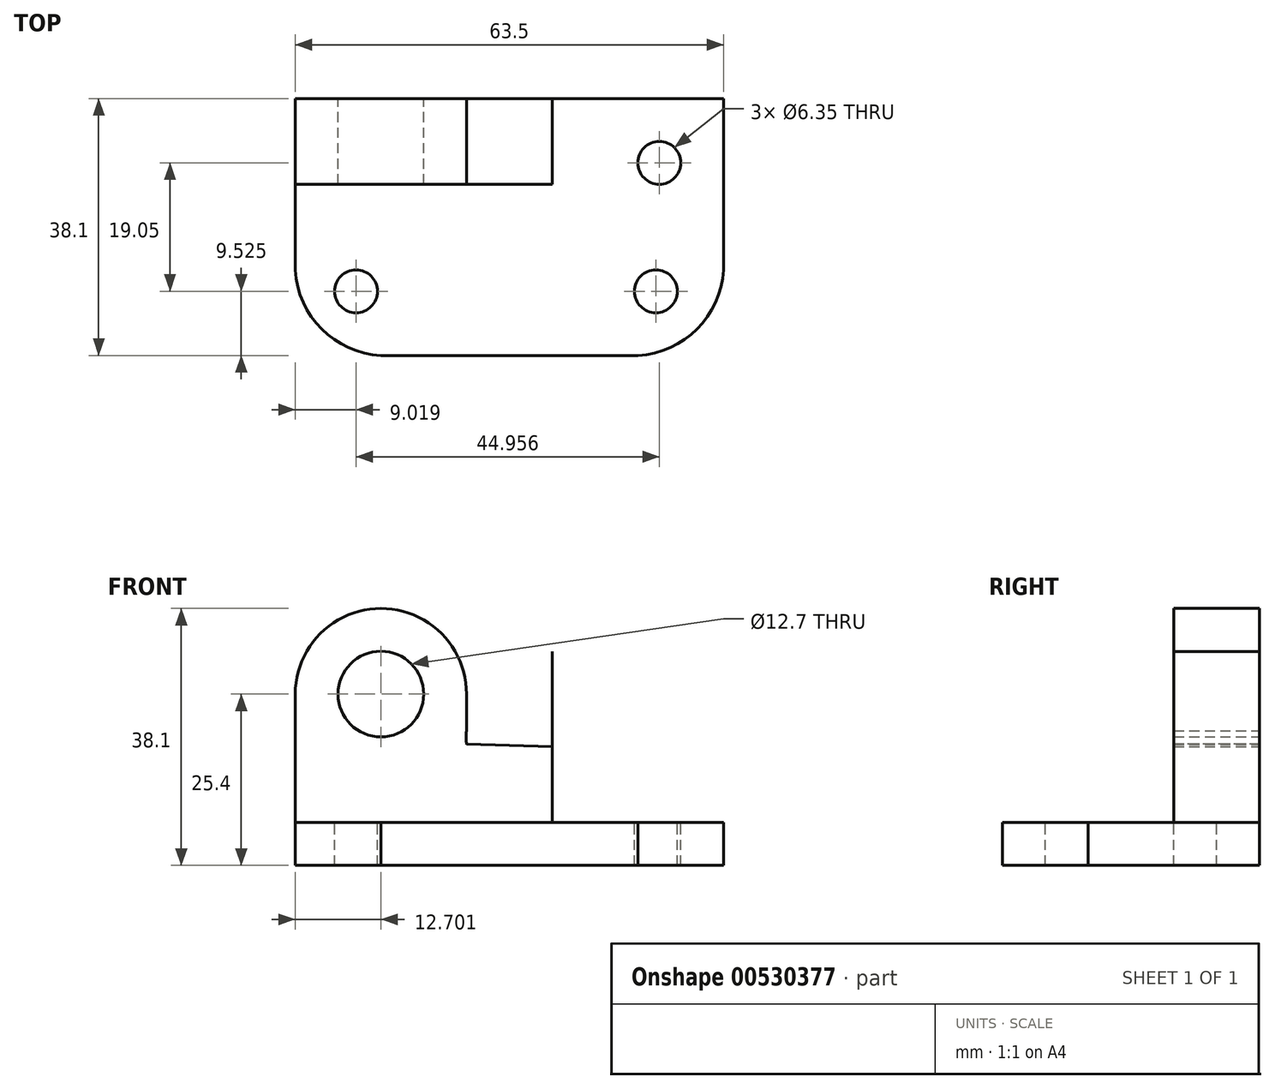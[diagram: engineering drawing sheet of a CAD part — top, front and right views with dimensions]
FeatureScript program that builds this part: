
annotation { "Feature Type Name" : "Feature", "Feature Type Description" : "" }
export const myFeature = defineFeature(function(context is Context, id is Id, definition is map)
    precondition{}
    {
        {
            var Q0;
            Q0=qCreatedBy(makeId("Front.planeOp"),FACE);
            var sketch = newSketch(context, id + "F0", { "sketchPlane" : qUnion([Q0])});
            skLineSegment(sketch, "E0", {"start": v(-21.45, 38.1) * mm, "end": v(-21.45, 0) * mm});
            skLineSegment(sketch, "E1", {"start": v(-21.45, 0) * mm, "end": v(42.05, 0) * mm});
            skLineSegment(sketch, "E2", {"start": v(42.05, 0) * mm, "end": v(42.05, 6.35) * mm});
            skLineSegment(sketch, "E3", {"start": v(42.05, 6.35) * mm, "end": v(16.65, 6.35) * mm});
            skLineSegment(sketch, "E4", {"start": v(16.65, 6.35) * mm, "end": v(16.65, 38.1) * mm});
            skLineSegment(sketch, "E5", {"start": v(16.65, 38.1) * mm, "end": v(-21.45, 38.1) * mm});
            skSolve(sketch);
        }
        {
            var Q0;
            Q0=makeQuery(id+"F0.imprint","IMPRINT",FACE,{"disambiguationData":[TD([[makeQuery(id+"F0.imprint","IMPRINT",EDGE,{"derivedFrom":sQuery(id+"F0.wireOp",EDGE,"E0")}),1.0]])]});
            extrude(context, id + "F1", {"entities" : qUnion([Q0]), "depth" : 38.1 * mm, "offsetDistance" : 25.4 * mm});
        }
        {
            var Q0;
            Q0=makeQuery(id+"F1.opExtrude","CAP_FACE",FACE,{"disambiguationData":[OSD([sQuery(id+"F0.wireOp",EDGE,"E0"),sQuery(id+"F0.wireOp",EDGE,"E1"),sQuery(id+"F0.wireOp",EDGE,"E2"),sQuery(id+"F0.wireOp",EDGE,"E3"),sQuery(id+"F0.wireOp",EDGE,"E4"),sQuery(id+"F0.wireOp",EDGE,"E5")])],"isStart":true});
            var sketch = newSketch(context, id + "F2", { "sketchPlane" : qUnion([Q0])});
            skSolve(sketch);
        }
        {
            var Q0;
            Q0=makeQuery(id+"F2.imprint","IMPRINT",FACE,{"disambiguationData":[TD([[makeQuery(id+"F2.imprint","IMPRINT",EDGE,{"derivedFrom":makeQuery(id+"F1.opExtrude","CAP_EDGE",EDGE,{"disambiguationData":[OSD([sQuery(id+"F0.wireOp",EDGE,"E0")])],"isStart":true})}),-1.0]])]});
            var sketch = newSketch(context, id + "F3", { "sketchPlane" : qUnion([Q0])});
            skLineSegment(sketch, "E6", {"start": v(-3.95, 0) * mm, "end": v(-3.95, 38.1) * mm});
            skArc(sketch, "E7", {"start": v(21.45, 25.4) * mm, "mid": v(8.75, 38.1) * mm, "end": v(-3.95, 25.4) * mm});
            skCircle(sketch, "E8", {"center": v(8.75, 25.4) * mm, "radius": 6.35 * mm});
            skSolve(sketch);
        }
        {
            var Q0;
            Q0=makeQuery(id+"F3.imprint","IMPRINT",FACE,{"disambiguationData":[TD([[makeQuery(id+"F3.imprint","IMPRINT",EDGE,{"derivedFrom":sQuery(id+"F3.wireOp",EDGE,"E8")}),1.0]])]});
            var Q1;
            {var subQ0=sQuery(id+"F3.wireOp",EDGE,"E7");var subQ1=makeQuery(id+"F2.imprint","IMPRINT",EDGE,{"derivedFrom":makeQuery(id+"F1.opExtrude","CAP_EDGE",EDGE,{"disambiguationData":[OSD([sQuery(id+"F0.wireOp",EDGE,"E0")])],"isStart":true})});var subQ2=makeQuery(id+"F3.imprint","INTERSECT",VERTEX,{"derivedFrom":[subQ1,subQ0]});Q1=makeQuery(id+"F3.imprint","IMPRINT",FACE,{"disambiguationData":[TD([[makeQuery(id+"F3.imprint","IMPRINT",EDGE,{"disambiguationData":[TD([[subQ2,-1.0]])],"derivedFrom":subQ0}),-1.0]])]});}
            var Q2;
            {var subQ0=sQuery(id+"F3.wireOp",EDGE,"E6");var subQ1=makeQuery(id+"F2.imprint","IMPRINT",EDGE,{"derivedFrom":makeQuery(id+"F1.opExtrude","CAP_EDGE",EDGE,{"disambiguationData":[OSD([sQuery(id+"F0.wireOp",EDGE,"E5")])],"isStart":true})});var subQ2=makeQuery(id+"F3.imprint","INTERSECT",VERTEX,{"derivedFrom":[subQ1,subQ0]});Q2=makeQuery(id+"F3.imprint","IMPRINT",FACE,{"disambiguationData":[TD([[makeQuery(id+"F3.imprint","IMPRINT",EDGE,{"disambiguationData":[TD([[subQ2,1.0]])],"derivedFrom":subQ0}),-1.0]])]});}
            extrude(context, id + "F4", {"entities" : qUnion([Q0, Q1, Q2]), "operationType" : NewBodyOperationType.REMOVE, "endBound" : BoundingType.THROUGH_ALL, "oppositeDirection" : true, "depth" : 25.4 * mm, "offsetDistance" : 25.4 * mm});
        }
        {
            var Q0;
            Q0=makeQuery(id+"F1.opExtrude","SWEPT_FACE",FACE,{"disambiguationData":[OSD([sQuery(id+"F0.wireOp",EDGE,"E4")])]});
            var sketch = newSketch(context, id + "F5", { "sketchPlane" : qUnion([Q0])});
            skLineSegment(sketch, "E9", {"start": v(-12.7, 38.1) * mm, "end": v(-12.7, 6.35) * mm});
            skLineSegment(sketch, "E10", {"start": v(-12.7, 6.35) * mm, "end": v(-38.1, 6.35) * mm});
            skLineSegment(sketch, "E11", {"start": v(-38.1, 6.35) * mm, "end": v(-38.1, 38.1) * mm});
            skLineSegment(sketch, "E12", {"start": v(-38.1, 38.1) * mm, "end": v(-12.7, 38.1) * mm});
            skSolve(sketch);
        }
        {
            var Q0;
            Q0=makeQuery(id+"F5.imprint","IMPRINT",FACE,{"disambiguationData":[TD([[makeQuery(id+"F5.imprint","IMPRINT",EDGE,{"derivedFrom":sQuery(id+"F5.wireOp",EDGE,"E9")}),-1.0]])]});
            extrude(context, id + "F6", {"entities" : qUnion([Q0]), "operationType" : NewBodyOperationType.REMOVE, "endBound" : BoundingType.THROUGH_ALL, "oppositeDirection" : true, "depth" : 25.4 * mm, "offsetDistance" : 25.4 * mm});
        }
        {
            var Q0;
            Q0=makeQuery(id+"F2.imprint","IMPRINT",FACE,{"disambiguationData":[TD([[makeQuery(id+"F2.imprint","IMPRINT",EDGE,{"derivedFrom":makeQuery(id+"F1.opExtrude","CAP_EDGE",EDGE,{"disambiguationData":[OSD([sQuery(id+"F0.wireOp",EDGE,"E0")])],"isStart":true})}),-1.0]])]});
            var sketch = newSketch(context, id + "F7", { "sketchPlane" : qUnion([Q0])});
            skCircle(sketch, "E13", {"center": v(-16.6, 19.03) * mm, "radius": 12.7 * mm});
            skLineSegment(sketch, "E14", {"start": v(-3.95, 17.91) * mm, "end": v(-3.95, 25.42) * mm});
            skSolve(sketch);
        }
        {
            var Q0;
            {var subQ0=sQuery(id+"F7.wireOp",EDGE,"E14");var subQ1=sQuery(id+"F7.wireOp",EDGE,"E13");var subQ3=makeQuery(id+"F7.imprint","INTERSECT",VERTEX,{"disambiguationData":[OD(1.0)],"derivedFrom":[subQ1,subQ0]});Q0=makeQuery(id+"F7.imprint","IMPRINT",FACE,{"disambiguationData":[TD([[makeQuery(id+"F7.imprint","IMPRINT",EDGE,{"disambiguationData":[TD([[subQ3,-1.0]])],"derivedFrom":subQ1}),1.0]])]});}
            var Q1;
            Q1=sQuery(id+"F7.wireOp",EDGE,"E13");
            extrude(context, id + "F8", {"entities" : qUnion([Q0]), "operationType" : NewBodyOperationType.REMOVE, "surfaceEntities" : qUnion([Q1]), "endBound" : BoundingType.THROUGH_ALL, "oppositeDirection" : true, "depth" : 25.4 * mm, "offsetDistance" : 25.4 * mm});
        }
        {
            var Q0;
            Q0=makeQuery(id+"F2.imprint","IMPRINT",FACE,{"disambiguationData":[TD([[makeQuery(id+"F2.imprint","IMPRINT",EDGE,{"derivedFrom":makeQuery(id+"F1.opExtrude","CAP_EDGE",EDGE,{"disambiguationData":[OSD([sQuery(id+"F0.wireOp",EDGE,"E0")])],"isStart":true})}),-1.0]])]});
            var sketch = newSketch(context, id + "F9", { "sketchPlane" : qUnion([Q0])});
            skLineSegment(sketch, "E15", {"start": v(-3.94, 25.4) * mm, "end": v(-3.94, 18) * mm});
            skLineSegment(sketch, "E16", {"start": v(-3.94, 25.4) * mm, "end": v(-3.95, 38.1) * mm});
            skLineSegment(sketch, "E17", {"start": v(-3.95, 38.1) * mm, "end": v(-16.65, 38.1) * mm});
            skLineSegment(sketch, "E18", {"start": v(-16.65, 38.1) * mm, "end": v(-16.65, 31.73) * mm});
            skLineSegment(sketch, "E19", {"start": v(-16.65, 31.73) * mm, "end": v(-16.64, 17.62) * mm});
            skLineSegment(sketch, "E20", {"start": v(-16.64, 17.62) * mm, "end": v(-3.94, 18) * mm});
            skSolve(sketch);
        }
        {
            var Q0;
            Q0 = qSketchRegion(id + "F9", true);
            extrude(context, id + "F10", {"entities" : qUnion([Q0]), "operationType" : NewBodyOperationType.REMOVE, "endBound" : BoundingType.THROUGH_ALL, "oppositeDirection" : true, "depth" : 25.4 * mm, "offsetDistance" : 25.4 * mm});
        }
        {
            var Q0;
            {var subQ0=sQuery(id+"F0.wireOp",EDGE,"E0");var subQ1=sQuery(id+"F0.wireOp",EDGE,"E3");Q0=makeQuery(id+"F8.boolean.opBoolean","SPLIT",FACE,{"disambiguationData":[TD([makeQuery(id+"F1.opExtrude","SWEPT_FACE",FACE,{"disambiguationData":[OSD([subQ0])]})])],"derivedFrom":makeQuery(id+"F6.boolean.opBoolean","MERGE",FACE,{"derivedFrom":[makeQuery(id+"F1.opExtrude","SWEPT_FACE",FACE,{"disambiguationData":[OSD([subQ1])]}),makeQuery(id+"F6.opExtrude","SWEPT_FACE",FACE,{"disambiguationData":[OSD([sQuery(id+"F5.wireOp",EDGE,"E10")])]})]})});}
            var sketch = newSketch(context, id + "F11", { "sketchPlane" : qUnion([Q0])});
            skArc(sketch, "E21", {"start": v(-21.45, -25.4) * mm, "mid": v(-17.52, -34.17) * mm, "end": v(-8.75, -38.1) * mm});
            skSolve(sketch);
        }
        {
            var Q0;
            {var subQ2=sQuery(id+"F0.wireOp",EDGE,"E3");var subQ3=sQuery(id+"F0.wireOp",EDGE,"E2");Q0=makeQuery(id+"F8.boolean.opBoolean","SPLIT",FACE,{"disambiguationData":[TD([makeQuery(id+"F1.opExtrude","SWEPT_FACE",FACE,{"disambiguationData":[OSD([subQ3])]})])],"derivedFrom":makeQuery(id+"F6.boolean.opBoolean","MERGE",FACE,{"derivedFrom":[makeQuery(id+"F1.opExtrude","SWEPT_FACE",FACE,{"disambiguationData":[OSD([subQ2])]}),makeQuery(id+"F6.opExtrude","SWEPT_FACE",FACE,{"disambiguationData":[OSD([sQuery(id+"F5.wireOp",EDGE,"E10")])]})]})});}
            var sketch = newSketch(context, id + "F12", { "sketchPlane" : qUnion([Q0])});
            skArc(sketch, "E22", {"start": v(29.35, -38.1) * mm, "mid": v(38.12, -34.17) * mm, "end": v(42.05, -25.4) * mm});
            skSolve(sketch);
        }
        {
            var Q0;
            {var subQ0=sQuery(id+"F12.wireOp",EDGE,"E22");Q0=makeQuery(id+"F12.imprint","IMPRINT",FACE,{"disambiguationData":[TD([[makeQuery(id+"F12.imprint","IMPRINT",EDGE,{"derivedFrom":subQ0}),-1.0]])]});}
            var Q1;
            {var subQ0=sQuery(id+"F11.wireOp",EDGE,"E21");Q1=makeQuery(id+"F11.imprint","IMPRINT",FACE,{"disambiguationData":[TD([[makeQuery(id+"F11.imprint","IMPRINT",EDGE,{"derivedFrom":subQ0}),-1.0]])]});}
            extrude(context, id + "F13", {"entities" : qUnion([Q0, Q1]), "operationType" : NewBodyOperationType.REMOVE, "endBound" : BoundingType.THROUGH_ALL, "oppositeDirection" : true, "depth" : 25.4 * mm, "offsetDistance" : 25.4 * mm});
        }
        {
            var Q0;
            {var subQ2=sQuery(id+"F0.wireOp",EDGE,"E3");var subQ3=sQuery(id+"F0.wireOp",EDGE,"E2");Q0=makeQuery(id+"F8.boolean.opBoolean","SPLIT",FACE,{"disambiguationData":[TD([makeQuery(id+"F1.opExtrude","SWEPT_FACE",FACE,{"disambiguationData":[OSD([subQ3])]})])],"derivedFrom":makeQuery(id+"F6.boolean.opBoolean","MERGE",FACE,{"derivedFrom":[makeQuery(id+"F1.opExtrude","SWEPT_FACE",FACE,{"disambiguationData":[OSD([subQ2])]}),makeQuery(id+"F6.opExtrude","SWEPT_FACE",FACE,{"disambiguationData":[OSD([sQuery(id+"F5.wireOp",EDGE,"E10")])]})]})});}
            var sketch = newSketch(context, id + "F14", { "sketchPlane" : qUnion([Q0])});
            skCircle(sketch, "E23", {"center": v(32.53, -9.52) * mm, "radius": 3.18 * mm});
            skCircle(sketch, "E24", {"center": v(-12.43, -28.58) * mm, "radius": 3.18 * mm});
            skCircle(sketch, "E25", {"center": v(32.02, -28.57) * mm, "radius": 3.18 * mm});
            skSolve(sketch);
        }
        {
            var Q0;
            Q0=makeQuery(id+"F14.imprint","IMPRINT",FACE,{"disambiguationData":[TD([[makeQuery(id+"F14.imprint","IMPRINT",EDGE,{"derivedFrom":sQuery(id+"F14.wireOp",EDGE,"E24")}),1.0]])]});
            var Q1;
            Q1=makeQuery(id+"F14.imprint","IMPRINT",FACE,{"disambiguationData":[TD([[makeQuery(id+"F14.imprint","IMPRINT",EDGE,{"derivedFrom":sQuery(id+"F14.wireOp",EDGE,"E25")}),1.0]])]});
            var Q2;
            Q2=makeQuery(id+"F14.imprint","IMPRINT",FACE,{"disambiguationData":[TD([[makeQuery(id+"F14.imprint","IMPRINT",EDGE,{"derivedFrom":sQuery(id+"F14.wireOp",EDGE,"E23")}),1.0]])]});
            extrude(context, id + "F15", {"entities" : qUnion([Q0, Q1, Q2]), "operationType" : NewBodyOperationType.REMOVE, "endBound" : BoundingType.THROUGH_ALL, "oppositeDirection" : true, "depth" : 25.4 * mm, "offsetDistance" : 25.4 * mm});
        }
    });
